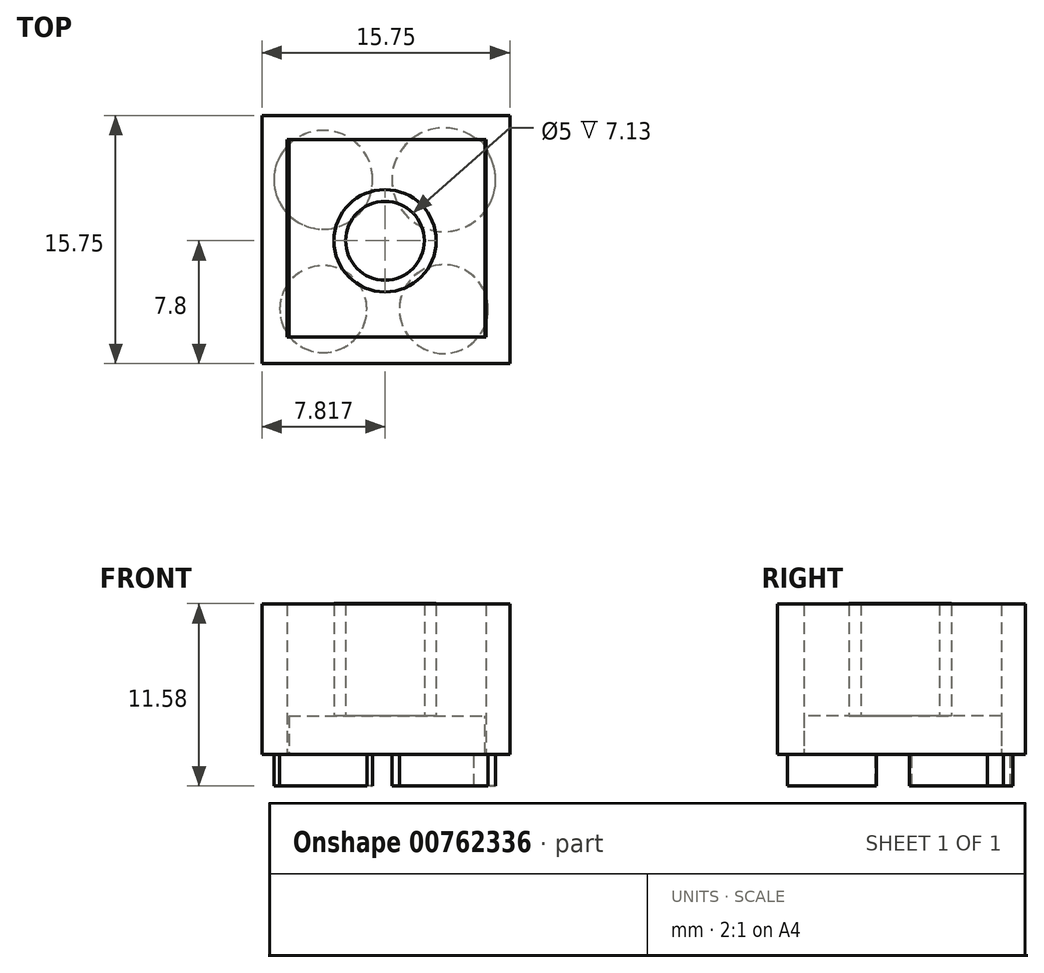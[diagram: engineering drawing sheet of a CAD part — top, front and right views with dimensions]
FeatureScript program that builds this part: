
annotation { "Feature Type Name" : "Feature", "Feature Type Description" : "" }
export const myFeature = defineFeature(function(context is Context, id is Id, definition is map)
    precondition{}
    {
        {
            var Q0;
            Q0=qCreatedBy(makeId("Top.planeOp"),FACE);
            var sketch = newSketch(context, id + "F0", { "sketchPlane" : qUnion([Q0])});
            skLineSegment(sketch, "E0.bottom", {"start": v(-10.1, 9.93) * mm, "end": v(5.64, 9.93) * mm});
            skLineSegment(sketch, "E0.top", {"start": v(-10.1, -5.82) * mm, "end": v(5.64, -5.82) * mm});
            skLineSegment(sketch, "E0.left", {"start": v(-10.1, 9.93) * mm, "end": v(-10.1, -5.82) * mm});
            skLineSegment(sketch, "E0.right", {"start": v(5.64, 9.93) * mm, "end": v(5.64, -5.82) * mm});
            skSolve(sketch);
        }
        {
            var Q0;
            Q0 = qSketchRegion(id + "F0", true);
            extrude(context, id + "F1", {"entities" : qUnion([Q0]), "depth" : 9.55 * mm, "offsetDistance" : 25 * mm});
        }
        {
            var Q0;
            Q0=qCreatedBy(makeId("Top.planeOp"),FACE);
            var sketch = newSketch(context, id + "F2", { "sketchPlane" : qUnion([Q0])});
            skCircle(sketch, "E1", {"center": v(2.95, 7.23) * mm, "radius": 1.36 * mm});
            skLineSegment(sketch, "E2", {"start": v(-7.96, 8.45) * mm, "end": v(-7.96, 8.42) * mm});
            skLineSegment(sketch, "E3", {"start": v(-9.35, 7.11) * mm, "end": v(-9.01, 7.08) * mm});
            skArc(sketch, "E4", {"start": v(-7.96, 8.45) * mm, "mid": v(-7.96, 8.45) * mm, "end": v(-7.97, 8.45) * mm});
            skPoint(sketch, "E5.orphan", {"position": v(-10.55, 7.23) * mm});
            skPoint(sketch, "E6.end.orphan", {"position": v(4.36, 7.23) * mm});
            skCircle(sketch, "E7", {"center": v(-6.21, 5.85) * mm, "radius": 3.14 * mm});
            skCircle(sketch, "E8", {"center": v(1.44, 5.85) * mm, "radius": 3.3 * mm});
            skCircle(sketch, "E9", {"center": v(-6.21, -2.36) * mm, "radius": 2.77 * mm});
            skCircle(sketch, "E10", {"center": v(1.44, -2.36) * mm, "radius": 2.82 * mm});
            skSolve(sketch);
        }
        {
            var Q0;
            Q0 = qSketchRegion(id + "F2", true);
            extrude(context, id + "F3", {"entities" : qUnion([Q0]), "operationType" : NewBodyOperationType.ADD, "oppositeDirection" : true, "depth" : 2 * mm, "offsetDistance" : 25 * mm});
        }
        {
            var Q0;
            Q0=qCreatedBy(makeId("Top.planeOp"),FACE);
            var sketch = newSketch(context, id + "F4", { "sketchPlane" : qUnion([Q0])});
            skLineSegment(sketch, "E11.bottom", {"start": v(-8.51, 8.4) * mm, "end": v(4.12, 8.4) * mm});
            skLineSegment(sketch, "E11.top", {"start": v(-8.51, -4.15) * mm, "end": v(4.12, -4.15) * mm});
            skLineSegment(sketch, "E11.left", {"start": v(-8.51, 8.4) * mm, "end": v(-8.51, -4.15) * mm});
            skLineSegment(sketch, "E11.right", {"start": v(4.12, 8.4) * mm, "end": v(4.12, -4.15) * mm});
            skPoint(sketch, "E12.end.orphan", {"position": v(-2.54, 8.4) * mm});
            skPoint(sketch, "E13.start.orphan", {"position": v(5.68, 2.2) * mm});
            skPoint(sketch, "E14.end.orphan", {"position": v(-8.51, 2.2) * mm});
            skPoint(sketch, "E15.start.orphan", {"position": v(-2.54, -5.75) * mm});
            skSolve(sketch);
        }
        {
            var Q0;
            Q0 = qSketchRegion(id + "F4", true);
            extrude(context, id + "F5", {"entities" : qUnion([Q0]), "operationType" : NewBodyOperationType.REMOVE, "depth" : 10 * mm, "offsetDistance" : 25 * mm});
        }
        {
            var Q0;
            Q0=qCreatedBy(makeId("Top.planeOp"),FACE);
            var sketch = newSketch(context, id + "F6", { "sketchPlane" : qUnion([Q0])});
            skLineSegment(sketch, "E16.bottom", {"start": v(-8.4, 8.4) * mm, "end": v(4.05, 8.4) * mm});
            skLineSegment(sketch, "E16.top", {"start": v(-8.4, -4.22) * mm, "end": v(4.05, -4.22) * mm});
            skLineSegment(sketch, "E16.left", {"start": v(-8.4, 8.4) * mm, "end": v(-8.4, -4.22) * mm});
            skLineSegment(sketch, "E16.right", {"start": v(4.05, 8.4) * mm, "end": v(4.05, -4.22) * mm});
            skSolve(sketch);
        }
        {
            var Q0;
            Q0 = qSketchRegion(id + "F6", true);
            extrude(context, id + "F7", {"entities" : qUnion([Q0]), "operationType" : NewBodyOperationType.ADD, "depth" : 2.45 * mm, "offsetDistance" : 25 * mm});
        }
        {
            var Q0;
            Q0=qCreatedBy(makeId("Top.planeOp"),FACE);
            var sketch = newSketch(context, id + "F8", { "sketchPlane" : qUnion([Q0])});
            skCircle(sketch, "E17", {"center": v(-2.3, 1.98) * mm, "radius": 2.5 * mm});
            skCircle(sketch, "E18", {"center": v(-2.3, 1.98) * mm, "radius": 3.25 * mm});
            skSolve(sketch);
        }
        {
            var Q0;
            Q0 = qSketchRegion(id + "F8", true);
            extrude(context, id + "F9", {"entities" : qUnion([Q0]), "operationType" : NewBodyOperationType.ADD, "depth" : 9.58 * mm, "offsetDistance" : 25 * mm});
        }
    });
